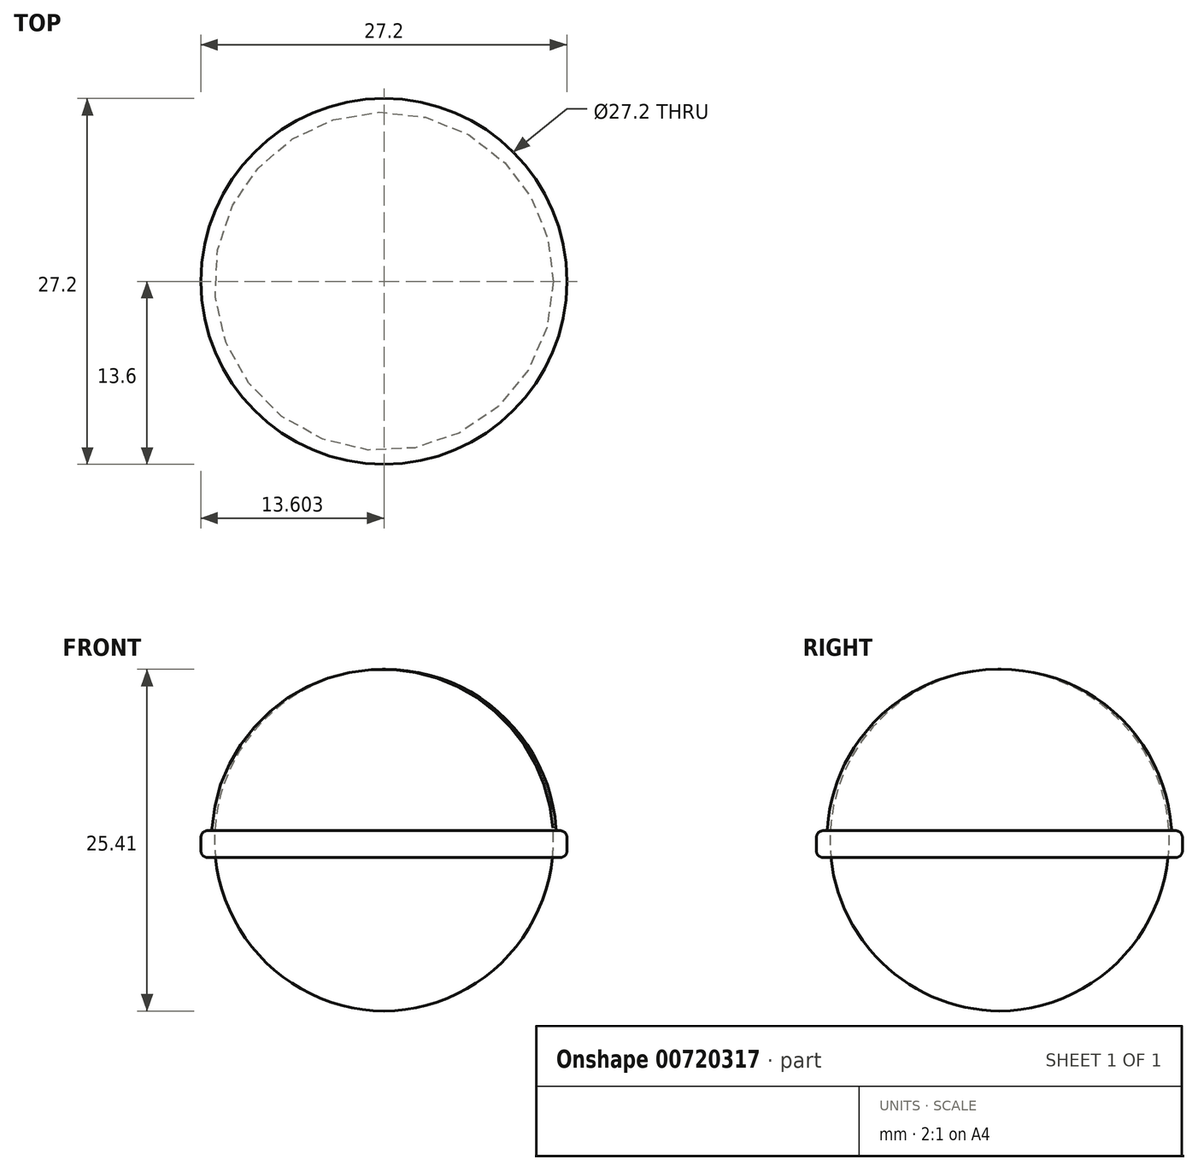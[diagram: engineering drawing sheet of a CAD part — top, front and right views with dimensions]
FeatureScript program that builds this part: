
annotation { "Feature Type Name" : "Feature", "Feature Type Description" : "" }
export const myFeature = defineFeature(function(context is Context, id is Id, definition is map)
    precondition{}
    {
        {
            var Q0;
            Q0=qCreatedBy(makeId("Front.planeOp"),FACE);
            var sketch = newSketch(context, id + "F0", { "sketchPlane" : qUnion([Q0])});
            skLineSegment(sketch, "E0", {"start": v(-8.32, -3.94) * mm, "end": v(5.28, -3.94) * mm});
            skLineSegment(sketch, "E1", {"start": v(5.28, -3.94) * mm, "end": v(5.28, -1.94) * mm});
            skLineSegment(sketch, "E2", {"start": v(5.28, -1.94) * mm, "end": v(4.48, -1.94) * mm});
            skLineSegment(sketch, "E3", {"start": v(-8.32, -3.94) * mm, "end": v(-8.32, 10.06) * mm});
            skArc(sketch, "E4", {"start": v(4.48, -1.94) * mm, "mid": v(0.49, 6.63) * mm, "end": v(-8.32, 10.06) * mm});
            skSolve(sketch);
        }
        {
            var Q0;
            Q0=makeQuery(id+"F0.imprint","IMPRINT",FACE,{"disambiguationData":[TD([[makeQuery(id+"F0.imprint","IMPRINT",EDGE,{"derivedFrom":sQuery(id+"F0.wireOp",EDGE,"E0")}),1.0]])]});
            var Q1;
            Q1=sQuery(id+"F0.wireOp",EDGE,"E3");
            revolve(context, id + "F1", {"surfaceOperationType" : NewSurfaceOperationType.NEW, "entities" : qUnion([Q0]), "axis" : qUnion([Q1]), "revolveType" : RevolveType.FULL});
        }
        {
            var Q0;
            Q0=makeQuery(id+"F1.opRevolve","SWEPT_EDGE",EDGE,{"disambiguationData":[OSD([sQuery(id+"F0.wireOp",EDGE,"E0"),sQuery(id+"F0.wireOp",EDGE,"E1")])]});
            var Q1;
            Q1=makeQuery(id+"F1.opRevolve","SWEPT_EDGE",EDGE,{"disambiguationData":[OSD([sQuery(id+"F0.wireOp",EDGE,"E1"),sQuery(id+"F0.wireOp",EDGE,"E2")])]});
            fillet(context, id + "F2", {"entities" : qUnion([Q0, Q1]), "tangentPropagation" : true, "radius" : 0.5 * mm, "defaultsChanged" : true, "vertexSettings" : [], "allowEdgeOverflow" : false});
        }
        {
            var Q0;
            Q0=makeQuery(id+"F1.opRevolve","SWEPT_EDGE",EDGE,{"disambiguationData":[OSD([sQuery(id+"F0.wireOp",EDGE,"E2"),sQuery(id+"F0.wireOp",EDGE,"E4")])]});
            fillet(context, id + "F3", {"entities" : qUnion([Q0]), "tangentPropagation" : true, "radius" : 0.2 * mm, "defaultsChanged" : true, "vertexSettings" : [], "allowEdgeOverflow" : false});
        }
    });
